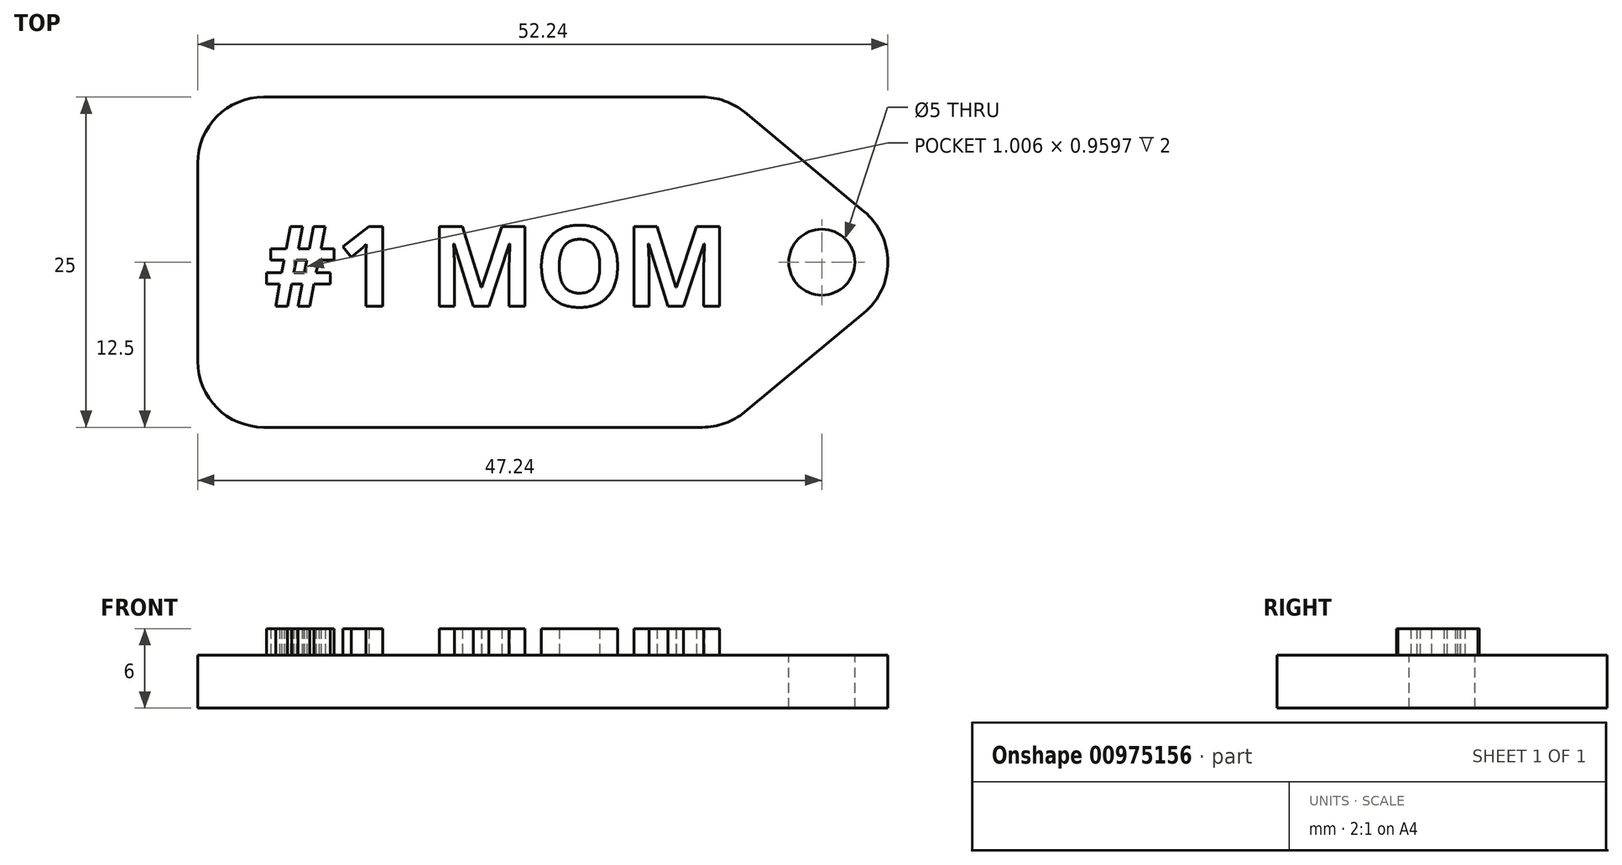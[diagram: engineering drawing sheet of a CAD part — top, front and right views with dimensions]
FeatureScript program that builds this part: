
annotation { "Feature Type Name" : "Feature", "Feature Type Description" : "" }
export const myFeature = defineFeature(function(context is Context, id is Id, definition is map)
    precondition{}
    {
        {
            var Q0;
            Q0=qCreatedBy(makeId("Top.planeOp"),FACE);
            var sketch = newSketch(context, id + "F0", { "sketchPlane" : qUnion([Q0])});
            skLineSegment(sketch, "E0.bottom", {"start": v(20, -12.5) * mm, "end": v(-20, -12.5) * mm});
            skLineSegment(sketch, "E0.top", {"start": v(20, 12.5) * mm, "end": v(-20, 12.5) * mm});
            skLineSegment(sketch, "E0.right", {"start": v(-20, -12.5) * mm, "end": v(-20, 12.5) * mm});
            skPoint(sketch, "E0.middle", {"position": v(0, 0) * mm});
            skPoint(sketch, "E1", {"position": v(35.07, 0) * mm});
            skLineSegment(sketch, "E2", {"start": v(20, 12.5) * mm, "end": v(35.07, 0) * mm});
            skLineSegment(sketch, "E3", {"start": v(20, -12.5) * mm, "end": v(35.07, 0) * mm});
            skSolve(sketch);
        }
        {
            var Q0;
            Q0 = qSketchRegion(id + "F0", true);
            extrude(context, id + "F1", {"entities" : qUnion([Q0]), "depth" : 4 * mm, "offsetDistance" : 25 * mm});
        }
        {
            var Q0;
            Q0=makeQuery(id+"F1.opExtrude","SWEPT_EDGE",EDGE,{"disambiguationData":[OSD([sQuery(id+"F0.wireOp",EDGE,"E2"),sQuery(id+"F0.wireOp",EDGE,"E3")])]});
            var Q1;
            Q1=makeQuery(id+"F1.opExtrude","SWEPT_EDGE",EDGE,{"disambiguationData":[OSD([sQuery(id+"F0.wireOp",EDGE,"E0.bottom"),sQuery(id+"F0.wireOp",EDGE,"E3")])]});
            fillet(context, id + "F2", {"entities" : qUnion([Q0, Q1]), "radius" : 5 * mm, "tangentPropagation" : true, "allowEdgeOverflow" : false});
        }
        {
            var Q0;
            Q0=makeQuery(id+"F1.opExtrude","SWEPT_EDGE",EDGE,{"disambiguationData":[OSD([sQuery(id+"F0.wireOp",EDGE,"E0.top"),sQuery(id+"F0.wireOp",EDGE,"E2")])]});
            fillet(context, id + "F3", {"entities" : qUnion([Q0]), "radius" : 5 * mm, "tangentPropagation" : true, "allowEdgeOverflow" : false});
        }
        {
            var Q0;
            Q0=makeQuery(id+"F1.opExtrude","SWEPT_EDGE",EDGE,{"disambiguationData":[OSD([sQuery(id+"F0.wireOp",EDGE,"E0.bottom"),sQuery(id+"F0.wireOp",EDGE,"E0.right")])]});
            var Q1;
            Q1=makeQuery(id+"F1.opExtrude","SWEPT_EDGE",EDGE,{"disambiguationData":[OSD([sQuery(id+"F0.wireOp",EDGE,"E0.top"),sQuery(id+"F0.wireOp",EDGE,"E0.right")])]});
            fillet(context, id + "F4", {"entities" : qUnion([Q0, Q1]), "radius" : 5 * mm, "tangentPropagation" : true, "allowEdgeOverflow" : false});
        }
        {
            var Q0;
            Q0=makeQuery(id+"F1.opExtrude","CAP_FACE",FACE,{"disambiguationData":[OSD([sQuery(id+"F0.wireOp",EDGE,"E0.bottom"),sQuery(id+"F0.wireOp",EDGE,"E0.top"),sQuery(id+"F0.wireOp",EDGE,"E0.right"),sQuery(id+"F0.wireOp",EDGE,"E2"),sQuery(id+"F0.wireOp",EDGE,"E3")])],"isStart":false});
            var sketch = newSketch(context, id + "F5", { "sketchPlane" : qUnion([Q0])});
            skPoint(sketch, "E4", {"position": v(0, 0) * mm});
            skPoint(sketch, "E5", {"position": v(27.24, 0) * mm});
            skSolve(sketch);
        }
        {
            var Q0;
            Q0=sQuery(id+"F5.wireOp",VERTEX,"E5");
            var Q1;
            Q1=makeQuery(id+"F1.opExtrude","SWEPT_BODY",BODY,{"disambiguationData":[OSD([sQuery(id+"F0.wireOp",EDGE,"E0.bottom"),sQuery(id+"F0.wireOp",EDGE,"E0.top"),sQuery(id+"F0.wireOp",EDGE,"E0.right"),sQuery(id+"F0.wireOp",EDGE,"E2"),sQuery(id+"F0.wireOp",EDGE,"E3")])]});
            hole(context, id + "F6", {"style" : HoleStyle.SIMPLE, "endStyle" : HoleEndStyle.THROUGH, "holeDiameter" : 5 * mm, "majorDiameter" : 5 * mm, "isTappedThrough" : true, "tappedDepth" : 12 * mm, "tapClearance" : 3, "locations" : qUnion([Q0]), "scope" : qUnion([Q1])});
        }
        {
            var Q0;
            Q0=makeQuery(id+"F1.opExtrude","CAP_FACE",FACE,{"disambiguationData":[OSD([sQuery(id+"F0.wireOp",EDGE,"E0.bottom"),sQuery(id+"F0.wireOp",EDGE,"E0.top"),sQuery(id+"F0.wireOp",EDGE,"E0.right"),sQuery(id+"F0.wireOp",EDGE,"E2"),sQuery(id+"F0.wireOp",EDGE,"E3")])],"isStart":false});
            var sketch = newSketch(context, id + "F7", { "sketchPlane" : qUnion([Q0])});
            skSolve(sketch);
        }
        {
            var Q0;
            {var subQ3=sQuery(id+"F0.wireOp",EDGE,"E3");Q0=makeQuery(id+"F7.imprint","IMPRINT",FACE,{"disambiguationData":[TD([[makeQuery(id+"F7.imprint","IMPRINT",EDGE,{"derivedFrom":makeQuery(id+"F1.opExtrude","CAP_EDGE",EDGE,{"disambiguationData":[OSD([subQ3])],"isStart":false})}),1.0]])]});}
            var sketch = newSketch(context, id + "F8", { "sketchPlane" : qUnion([Q0])});
            skText(sketch, "E6", { "text": "#1 MOM", "fontName": "OpenSans-Bold.ttf"});
            const initialGuessF8  = {"E6": [-0.01497, -0.00334, 1, 0, 0.0061]};
            skSetInitialGuess(sketch, initialGuessF8);
            skSolve(sketch);
        }
        {
            var Q0;
            Q0 = qSketchRegion(id + "F8", true);
            extrude(context, id + "F9", {"entities" : qUnion([Q0]), "operationType" : NewBodyOperationType.ADD, "depth" : 2 * mm, "offsetDistance" : 25 * mm});
        }
    });
